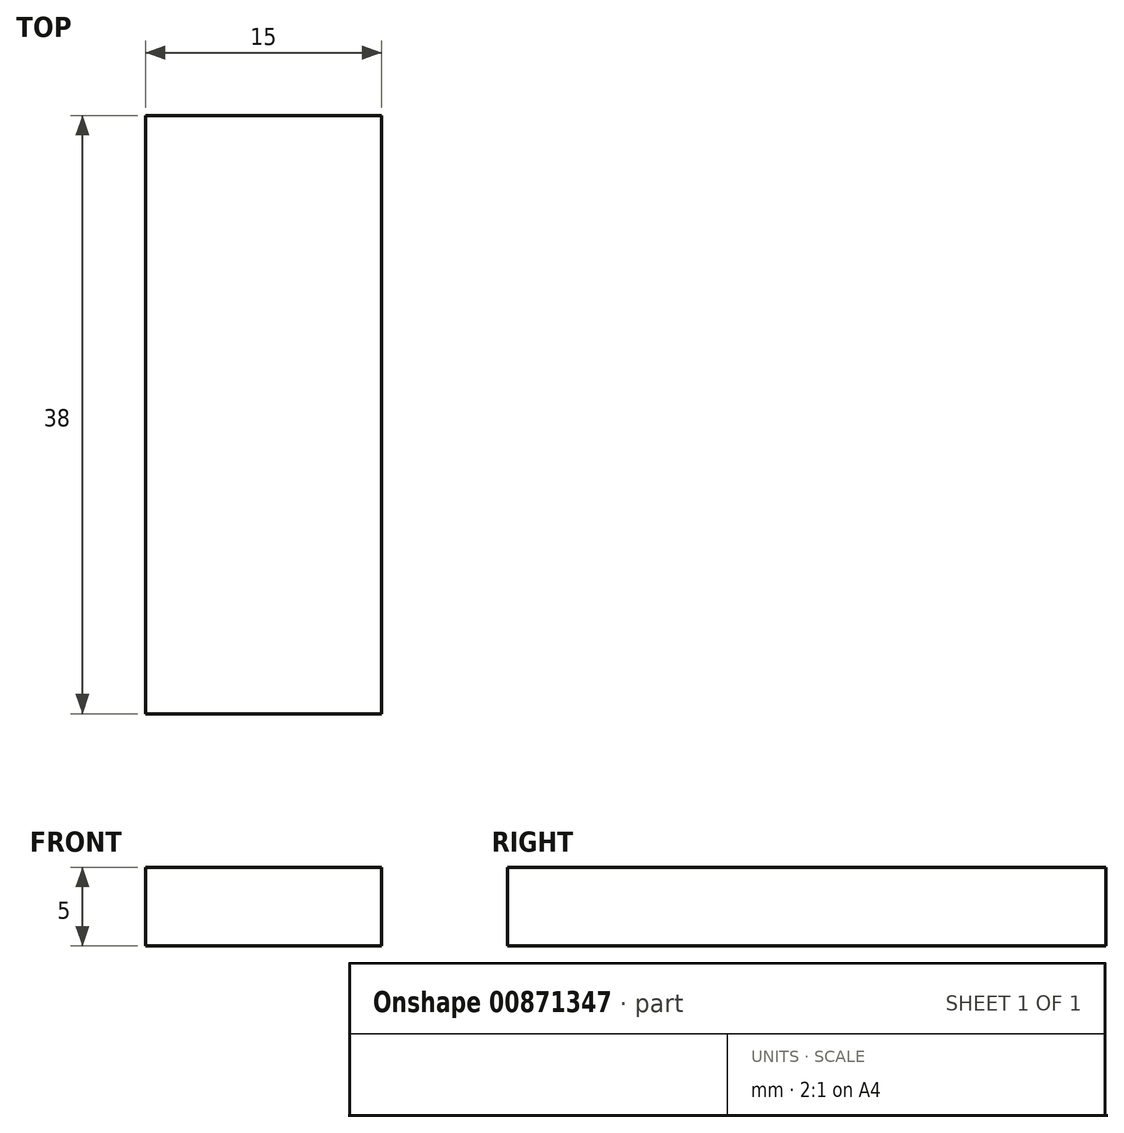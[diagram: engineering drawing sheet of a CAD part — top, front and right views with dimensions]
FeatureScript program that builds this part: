
annotation { "Feature Type Name" : "Feature", "Feature Type Description" : "" }
export const myFeature = defineFeature(function(context is Context, id is Id, definition is map)
    precondition{}
    {
        {
            var Q0;
            Q0=qCreatedBy(makeId("Top.planeOp"),FACE);
            var sketch = newSketch(context, id + "F0", { "sketchPlane" : qUnion([Q0])});
            skLineSegment(sketch, "E0.bottom", {"start": v(-6.06, 70.22) * mm, "end": v(8.94, 70.22) * mm});
            skLineSegment(sketch, "E0.top", {"start": v(-6.06, 32.22) * mm, "end": v(8.94, 32.22) * mm});
            skLineSegment(sketch, "E0.left", {"start": v(-6.06, 70.22) * mm, "end": v(-6.06, 32.22) * mm});
            skLineSegment(sketch, "E0.right", {"start": v(8.94, 70.22) * mm, "end": v(8.94, 32.22) * mm});
            skSolve(sketch);
        }
        {
            var Q0;
            Q0=makeQuery(id+"F0.imprint","IMPRINT",FACE,{"disambiguationData":[TD([[makeQuery(id+"F0.imprint","IMPRINT",EDGE,{"derivedFrom":sQuery(id+"F0.wireOp",EDGE,"E0.bottom")}),-1.0]])]});
            extrude(context, id + "F1", {"entities" : qUnion([Q0]), "depth" : 5 * mm, "offsetDistance" : 25 * mm});
        }
    });
